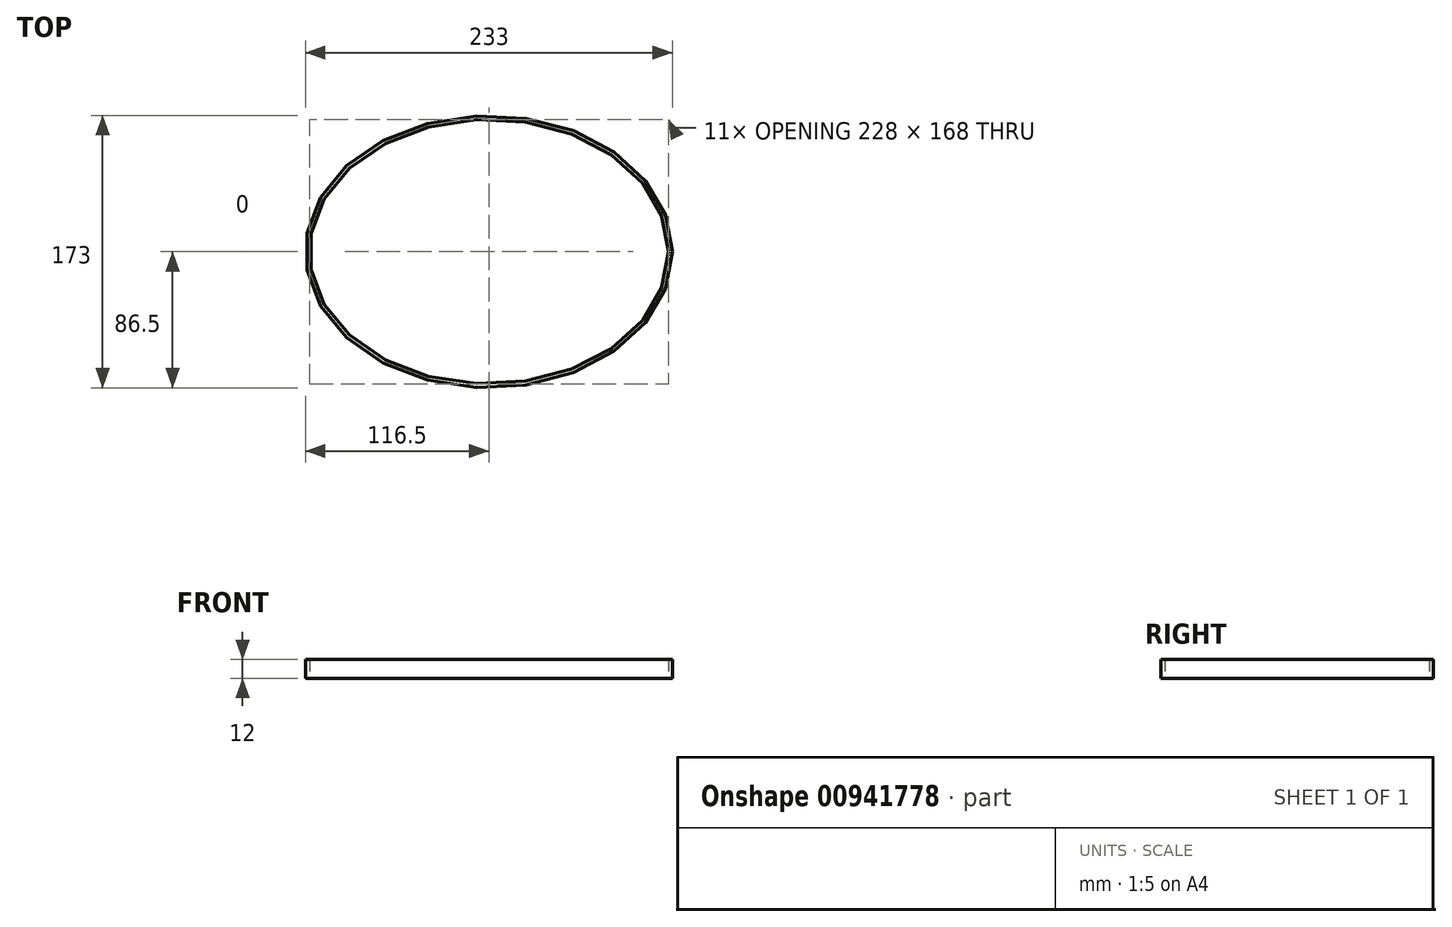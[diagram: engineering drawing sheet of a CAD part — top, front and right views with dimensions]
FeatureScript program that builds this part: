
annotation { "Feature Type Name" : "Feature", "Feature Type Description" : "" }
export const myFeature = defineFeature(function(context is Context, id is Id, definition is map)
    precondition{}
    {
        {
            var Q0;
            Q0=qCreatedBy(makeId("Top.planeOp"),FACE);
            var sketch = newSketch(context, id + "F0", { "sketchPlane" : qUnion([Q0])});
            skEllipse(sketch, "E0", {"center": v(0, 0) * mm, "majorRadius": 114 * mm, "minorRadius": 84 * mm, "majorAxis": v(1, 0)});
            skEllipse(sketch, "E1", {"center": v(0, 0) * mm, "majorRadius": 116.5 * mm, "minorRadius": 86.5 * mm, "majorAxis": v(1, 0)});
            skSolve(sketch);
        }
        {
            var Q0;
            Q0=qSketchRegion(id+"F0",true);
            extrude(context, id + "F1", {"entities" : qUnion([Q0]), "depth" : 12 * mm, "offsetDistance" : 25 * mm});
        }
    });
